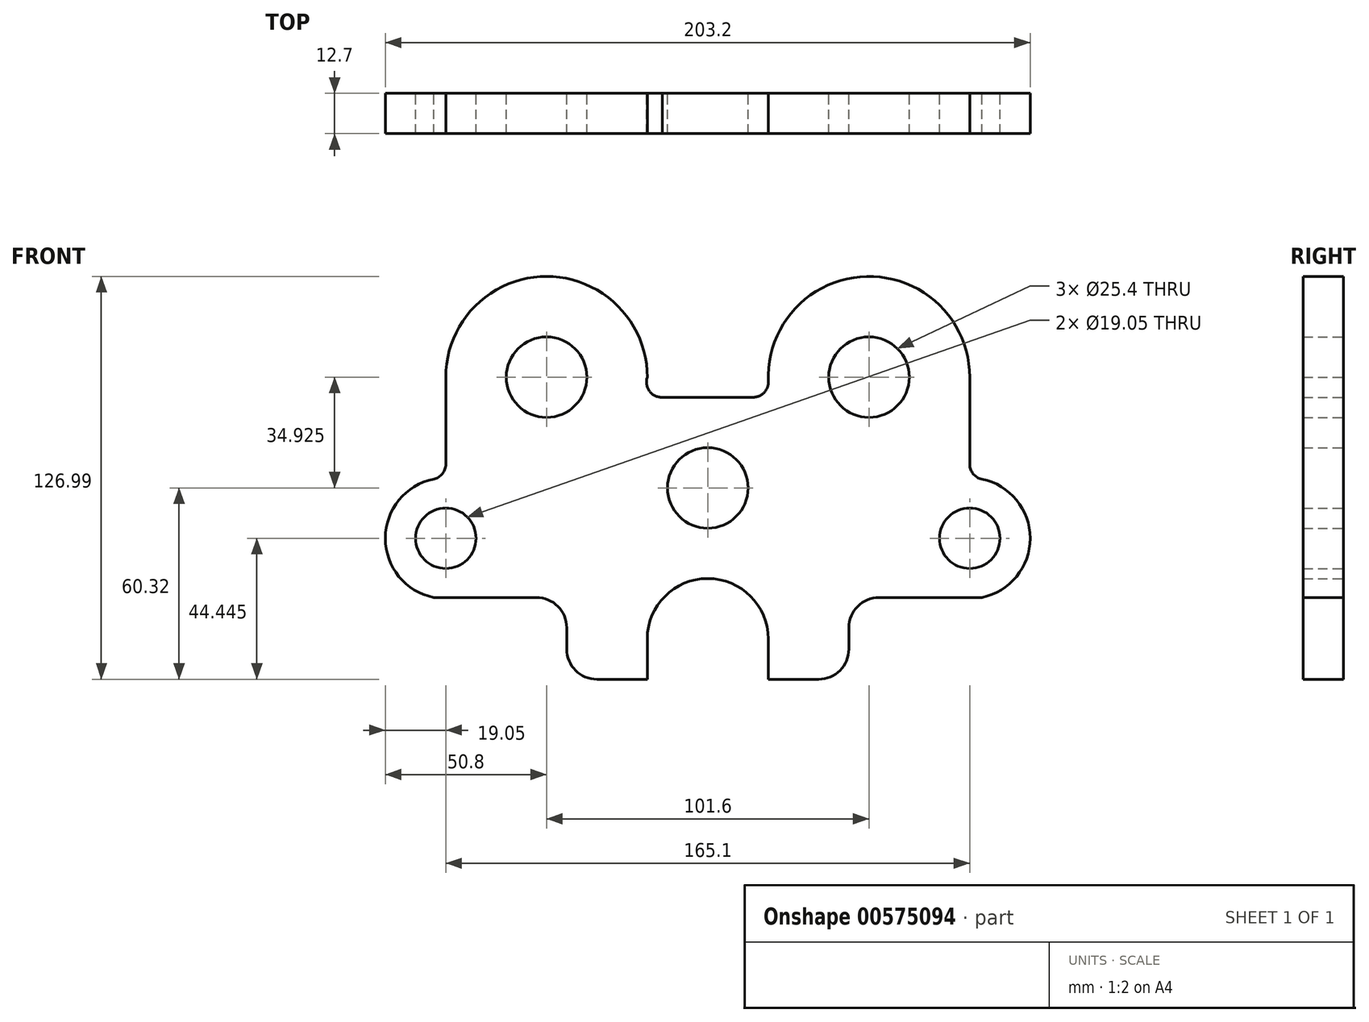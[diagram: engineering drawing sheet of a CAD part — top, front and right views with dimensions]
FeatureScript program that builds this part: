
annotation { "Feature Type Name" : "Feature", "Feature Type Description" : "" }
export const myFeature = defineFeature(function(context is Context, id is Id, definition is map)
    precondition{}
    {
        {
            var Q0;
            Q0=qCreatedBy(makeId("Front.planeOp"),FACE);
            var sketch = newSketch(context, id + "F0", { "sketchPlane" : qUnion([Q0])});
            skCircle(sketch, "E0", {"center": v(0, 0) * mm, "radius": 12.7 * mm});
            skArc(sketch, "E1.filletArc", {"start": v(14.37, 28.58) * mm, "mid": v(17.78, 30.06) * mm, "end": v(19.08, 33.54) * mm});
            skArc(sketch, "E2", {"start": v(19.08, 33.54) * mm, "mid": v(50.1, 66.67) * mm, "end": v(82.55, 34.93) * mm});
            skArc(sketch, "E3", {"start": v(86.36, -34.54) * mm, "mid": v(101.6, -15.88) * mm, "end": v(86.36, 2.8) * mm});
            skLineSegment(sketch, "E4", {"start": v(57.16, 34.12) * mm, "end": v(57.16, 34.12) * mm});
            skPoint(sketch, "E5", {"position": v(50.8, 66.67) * mm});
            skPoint(sketch, "E6", {"position": v(101.6, -15.88) * mm});
            skCircle(sketch, "E7", {"center": v(82.55, -15.88) * mm, "radius": 6.35 * mm});
            skArc(sketch, "E8.MirrorCS", {"start": v(-14.37, 28.58) * mm, "mid": v(-18.36, 30.49) * mm, "end": v(-19.05, 34.86) * mm});
            skArc(sketch, "E9.MirrorCS", {"start": v(-19.05, 34.86) * mm, "mid": v(-50.77, 66.67) * mm, "end": v(-82.55, 34.92) * mm});
            skArc(sketch, "E10.MirrorCS", {"start": v(-86.36, -34.54) * mm, "mid": v(-101.6, -15.88) * mm, "end": v(-86.36, 2.8) * mm});
            skCircle(sketch, "E11.MirrorC", {"center": v(-82.55, -15.88) * mm, "radius": 6.35 * mm});
            skCircle(sketch, "E12", {"center": v(50.8, 34.93) * mm, "radius": 12.7 * mm});
            skCircle(sketch, "E13", {"center": v(-50.8, 34.92) * mm, "radius": 12.7 * mm});
            skLineSegment(sketch, "E14", {"start": v(-14.37, 28.58) * mm, "end": v(14.37, 28.58) * mm});
            skPoint(sketch, "E15", {"position": v(-101.6, -15.88) * mm});
            skPoint(sketch, "E16", {"position": v(-50.83, 66.67) * mm});
            skPoint(sketch, "E16.positionSnap0", {"position": v(-50.77, 66.67) * mm});
            skLineSegment(sketch, "E17", {"start": v(-19.05, -60.33) * mm, "end": v(-19.05, -47.63) * mm});
            skLineSegment(sketch, "E18", {"start": v(19.05, -47.63) * mm, "end": v(19.05, -60.33) * mm});
            skArc(sketch, "E19", {"start": v(-19.05, -47.63) * mm, "mid": v(-13.47, -34.15) * mm, "end": v(0, -28.58) * mm});
            skArc(sketch, "E20", {"start": v(19.05, -47.63) * mm, "mid": v(13.47, -34.15) * mm, "end": v(0, -28.58) * mm});
            skLineSegment(sketch, "E21", {"start": v(19.05, -60.33) * mm, "end": v(34.93, -60.33) * mm});
            skLineSegment(sketch, "E22", {"start": v(-19.05, -60.33) * mm, "end": v(-34.92, -60.33) * mm});
            skLineSegment(sketch, "E23", {"start": v(-44.45, -50.8) * mm, "end": v(-44.45, -44.07) * mm});
            skLineSegment(sketch, "E24", {"start": v(44.45, -50.8) * mm, "end": v(44.45, -44.07) * mm});
            skLineSegment(sketch, "E25", {"start": v(53.98, -34.54) * mm, "end": v(86.36, -34.54) * mm});
            skLineSegment(sketch, "E26", {"start": v(-53.97, -34.54) * mm, "end": v(-86.36, -34.54) * mm});
            skPoint(sketch, "E27.visualSharp", {"position": v(-44.45, -60.33) * mm});
            skArc(sketch, "E27.filletArc", {"start": v(-44.45, -50.8) * mm, "mid": v(-41.66, -57.54) * mm, "end": v(-34.92, -60.33) * mm});
            skPoint(sketch, "E28.visualSharp", {"position": v(-44.45, -34.54) * mm});
            skArc(sketch, "E28.filletArc", {"start": v(-44.45, -44.07) * mm, "mid": v(-47.24, -37.33) * mm, "end": v(-53.97, -34.54) * mm});
            skPoint(sketch, "E29.visualSharp", {"position": v(44.45, -34.54) * mm});
            skArc(sketch, "E29.filletArc", {"start": v(53.98, -34.54) * mm, "mid": v(47.24, -37.33) * mm, "end": v(44.45, -44.07) * mm});
            skPoint(sketch, "E30.visualSharp", {"position": v(44.45, -60.33) * mm});
            skArc(sketch, "E30.filletArc", {"start": v(34.93, -60.32) * mm, "mid": v(41.66, -57.54) * mm, "end": v(44.45, -50.8) * mm});
            skLineSegment(sketch, "E31", {"start": v(82.55, 34.93) * mm, "end": v(82.55, 7.46) * mm});
            skLineSegment(sketch, "E32", {"start": v(-82.55, 7.46) * mm, "end": v(-82.55, 34.92) * mm});
            skArc(sketch, "E33.filletArc", {"start": v(-86.36, 2.8) * mm, "mid": v(-83.62, 4.44) * mm, "end": v(-82.55, 7.46) * mm});
            skArc(sketch, "E34.filletArc", {"start": v(82.55, 7.46) * mm, "mid": v(83.62, 4.44) * mm, "end": v(86.36, 2.8) * mm});
            skCircle(sketch, "E35.0", {"center": v(-82.55, -15.88) * mm, "radius": 9.52 * mm});
            skCircle(sketch, "E36.0", {"center": v(82.55, -15.88) * mm, "radius": 9.53 * mm});
            skSolve(sketch);
        }
        {
            var Q0;
            Q0=makeQuery(id+"F0.imprint","IMPRINT",FACE,{"disambiguationData":[TD([[makeQuery(id+"F0.imprint","IMPRINT",EDGE,{"derivedFrom":sQuery(id+"F0.wireOp",EDGE,"E0")}),-1.0]])]});
            extrude(context, id + "F1", {"entities" : qUnion([Q0]), "depth" : 12.7 * mm, "offsetDistance" : 25.4 * mm});
        }
    });
